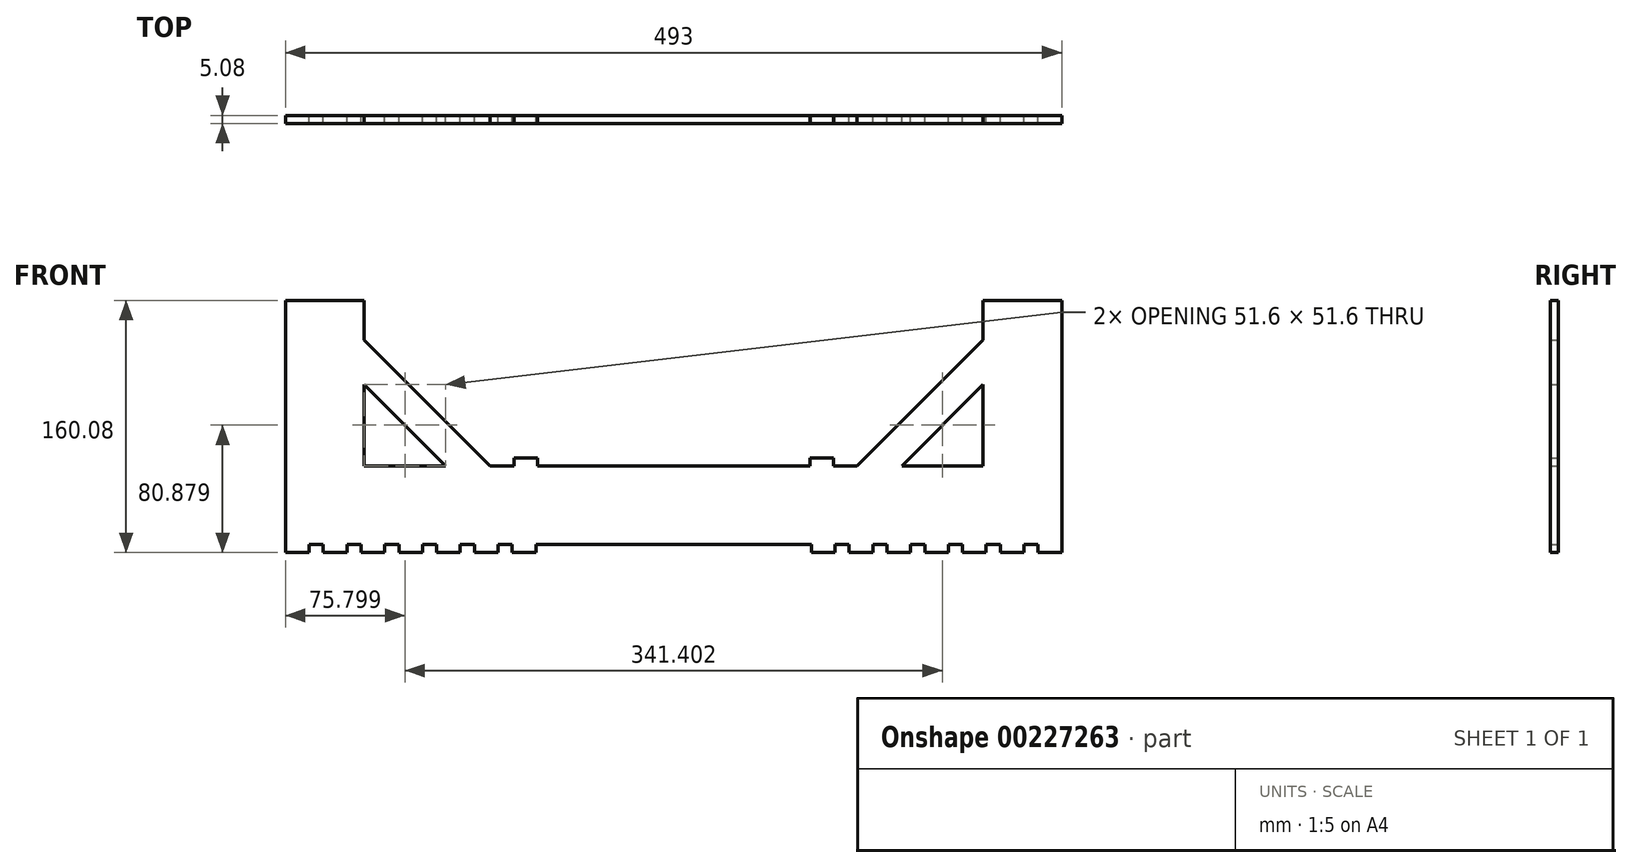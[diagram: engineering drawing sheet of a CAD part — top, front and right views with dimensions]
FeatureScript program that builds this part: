
annotation { "Feature Type Name" : "Feature", "Feature Type Description" : "" }
export const myFeature = defineFeature(function(context is Context, id is Id, definition is map)
    precondition{}
    {
        {
            var Q0;
            Q0=qCreatedBy(makeId("Front.planeOp"),FACE);
            var sketch = newSketch(context, id + "F0", { "sketchPlane" : qUnion([Q0])});
            skLineSegment(sketch, "E0", {"start": v(0, 0) * mm, "end": v(-246.5, 0) * mm});
            skLineSegment(sketch, "E1", {"start": v(-246.5, 0) * mm, "end": v(-246.5, 130) * mm});
            skLineSegment(sketch, "E2", {"start": v(-246.5, 130) * mm, "end": v(-196.5, 130) * mm});
            skLineSegment(sketch, "E3", {"start": v(-196.5, 130) * mm, "end": v(-196.5, 50) * mm});
            skLineSegment(sketch, "E4", {"start": v(-196.5, 50) * mm, "end": v(0, 50) * mm});
            skLineSegment(sketch, "E5", {"start": v(0, 50) * mm, "end": v(0, 0) * mm});
            skLineSegment(sketch, "E6", {"start": v(-196.5, 130) * mm, "end": v(-116.5, 50) * mm});
            skLineSegment(sketch, "E7", {"start": v(-196.5, 101.6) * mm, "end": v(-144.9, 50) * mm});
            skLineSegment(sketch, "E8", {"start": v(-246.5, 0) * mm, "end": v(-246.5, -5.08) * mm});
            skLineSegment(sketch, "E9", {"start": v(-246.5, -5.08) * mm, "end": v(-231.5, -5.08) * mm});
            skLineSegment(sketch, "E10", {"start": v(-231.5, -5.08) * mm, "end": v(-231.5, 0) * mm});
            skLineSegment(sketch, "E11.MirrorCS", {"start": v(196.5, 50) * mm, "end": v(0, 50) * mm});
            skLineSegment(sketch, "E12.MirrorCS", {"start": v(196.5, 130) * mm, "end": v(196.5, 50) * mm});
            skLineSegment(sketch, "E13.MirrorCS", {"start": v(196.5, 130) * mm, "end": v(116.5, 50) * mm});
            skLineSegment(sketch, "E14.MirrorCS", {"start": v(196.5, 101.6) * mm, "end": v(144.9, 50) * mm});
            skLineSegment(sketch, "E15.MirrorCS", {"start": v(246.5, 130) * mm, "end": v(196.5, 130) * mm});
            skLineSegment(sketch, "E16.MirrorCS", {"start": v(0, 0) * mm, "end": v(246.5, 0) * mm});
            skLineSegment(sketch, "E17.MirrorCS", {"start": v(246.5, 0) * mm, "end": v(246.5, 130) * mm});
            skLineSegment(sketch, "E18.1.0.0", {"start": v(-207.5, -5.08) * mm, "end": v(-207.5, 0) * mm});
            skLineSegment(sketch, "E18.1.0.1", {"start": v(-222.5, -5.08) * mm, "end": v(-207.5, -5.08) * mm});
            skLineSegment(sketch, "E18.1.0.2", {"start": v(-222.5, 0) * mm, "end": v(-222.5, -5.08) * mm});
            skLineSegment(sketch, "E18.2.0.0", {"start": v(-183.5, -5.08) * mm, "end": v(-183.5, 0) * mm});
            skLineSegment(sketch, "E18.2.0.1", {"start": v(-198.5, -5.08) * mm, "end": v(-183.5, -5.08) * mm});
            skLineSegment(sketch, "E18.2.0.2", {"start": v(-198.5, 0) * mm, "end": v(-198.5, -5.08) * mm});
            skLineSegment(sketch, "E18.3.0.0", {"start": v(-159.5, -5.08) * mm, "end": v(-159.5, 0) * mm});
            skLineSegment(sketch, "E18.3.0.1", {"start": v(-174.5, -5.08) * mm, "end": v(-159.5, -5.08) * mm});
            skLineSegment(sketch, "E18.3.0.2", {"start": v(-174.5, 0) * mm, "end": v(-174.5, -5.08) * mm});
            skLineSegment(sketch, "E18.4.0.0", {"start": v(-135.5, -5.08) * mm, "end": v(-135.5, 0) * mm});
            skLineSegment(sketch, "E18.4.0.1", {"start": v(-150.5, -5.08) * mm, "end": v(-135.5, -5.08) * mm});
            skLineSegment(sketch, "E18.4.0.2", {"start": v(-150.5, 0) * mm, "end": v(-150.5, -5.08) * mm});
            skLineSegment(sketch, "E18.5.0.0", {"start": v(-111.5, -5.08) * mm, "end": v(-111.5, 0) * mm});
            skLineSegment(sketch, "E18.5.0.1", {"start": v(-126.5, -5.08) * mm, "end": v(-111.5, -5.08) * mm});
            skLineSegment(sketch, "E18.5.0.2", {"start": v(-126.5, 0) * mm, "end": v(-126.5, -5.08) * mm});
            skLineSegment(sketch, "E18.6.0.0", {"start": v(-87.5, -5.08) * mm, "end": v(-87.5, 0) * mm});
            skLineSegment(sketch, "E18.6.0.1", {"start": v(-102.5, -5.08) * mm, "end": v(-87.5, -5.08) * mm});
            skLineSegment(sketch, "E18.6.0.2", {"start": v(-102.5, 0) * mm, "end": v(-102.5, -5.08) * mm});
            skLineSegment(sketch, "E18.direction1", {"start": v(-246.5, -5.08) * mm, "end": v(-222.5, -5.08) * mm, "construction": true});
            skLineSegment(sketch, "E19.MirrorCS", {"start": v(246.5, 0) * mm, "end": v(246.5, -5.08) * mm});
            skLineSegment(sketch, "E20.MirrorCS", {"start": v(231.5, -5.08) * mm, "end": v(231.5, 0) * mm});
            skLineSegment(sketch, "E21.MirrorCS", {"start": v(222.5, 0) * mm, "end": v(222.5, -5.08) * mm});
            skLineSegment(sketch, "E22.MirrorCS", {"start": v(222.5, -5.08) * mm, "end": v(207.5, -5.08) * mm});
            skLineSegment(sketch, "E23.MirrorCS", {"start": v(207.5, -5.08) * mm, "end": v(207.5, 0) * mm});
            skLineSegment(sketch, "E24.MirrorCS", {"start": v(198.5, 0) * mm, "end": v(198.5, -5.08) * mm});
            skLineSegment(sketch, "E25.MirrorCS", {"start": v(198.5, -5.08) * mm, "end": v(183.5, -5.08) * mm});
            skLineSegment(sketch, "E26.MirrorCS", {"start": v(183.5, -5.08) * mm, "end": v(183.5, 0) * mm});
            skLineSegment(sketch, "E27.MirrorCS", {"start": v(174.5, 0) * mm, "end": v(174.5, -5.08) * mm});
            skLineSegment(sketch, "E28.MirrorCS", {"start": v(174.5, -5.08) * mm, "end": v(159.5, -5.08) * mm});
            skLineSegment(sketch, "E29.MirrorCS", {"start": v(159.5, -5.08) * mm, "end": v(159.5, 0) * mm});
            skLineSegment(sketch, "E30.MirrorCS", {"start": v(150.5, 0) * mm, "end": v(150.5, -5.08) * mm});
            skLineSegment(sketch, "E31.MirrorCS", {"start": v(150.5, -5.08) * mm, "end": v(135.5, -5.08) * mm});
            skLineSegment(sketch, "E32.MirrorCS", {"start": v(135.5, -5.08) * mm, "end": v(135.5, 0) * mm});
            skLineSegment(sketch, "E33.MirrorCS", {"start": v(87.5, -5.08) * mm, "end": v(87.5, 0) * mm});
            skLineSegment(sketch, "E34.MirrorCS", {"start": v(102.5, -5.08) * mm, "end": v(87.5, -5.08) * mm});
            skLineSegment(sketch, "E35.MirrorCS", {"start": v(102.5, 0) * mm, "end": v(102.5, -5.08) * mm});
            skLineSegment(sketch, "E36.MirrorCS", {"start": v(111.5, -5.08) * mm, "end": v(111.5, 0) * mm});
            skLineSegment(sketch, "E37.MirrorCS", {"start": v(126.5, 0) * mm, "end": v(126.5, -5.08) * mm});
            skLineSegment(sketch, "E38.MirrorCS", {"start": v(126.5, -5.08) * mm, "end": v(111.5, -5.08) * mm});
            skLineSegment(sketch, "E39", {"start": v(231.5, -5.08) * mm, "end": v(246.5, -5.08) * mm});
            skSolve(sketch);
        }
        {
            var Q0;
            Q0 = qSketchRegion(id + "F0", true);
            extrude(context, id + "F1", {"entities" : qUnion([Q0]), "depth" : 5.08 * mm});
        }
        {
            var Q0;
            Q0=makeQuery(id+"F1.opExtrude","SWEPT_FACE",FACE,{"disambiguationData":[OSD([sQuery(id+"F0.wireOp",EDGE,"E2")])]});
            var Q1;
            Q1=makeQuery(id+"F1.opExtrude","SWEPT_FACE",FACE,{"disambiguationData":[OSD([sQuery(id+"F0.wireOp",EDGE,"E15.MirrorCS")])]});
            extrude(context, id + "F2", {"entities" : qUnion([Q0, Q1]), "operationType" : NewBodyOperationType.ADD, "depth" : 25 * mm});
        }
        {
            var Q0;
            Q0=makeQuery(id+"F1.opExtrude","SWEPT_FACE",FACE,{"disambiguationData":[OSD([sQuery(id+"F0.wireOp",EDGE,"E4"),sQuery(id+"F0.wireOp",EDGE,"E11.MirrorCS")])]});
            var sketch = newSketch(context, id + "F3", { "sketchPlane" : qUnion([Q0])});
            skLineSegment(sketch, "E40.bottom", {"start": v(101.5, -5.08) * mm, "end": v(86.5, -5.08) * mm});
            skLineSegment(sketch, "E40.top", {"start": v(101.5, 0) * mm, "end": v(86.5, 0) * mm});
            skLineSegment(sketch, "E40.right", {"start": v(86.5, -5.08) * mm, "end": v(86.5, 0) * mm});
            skLineSegment(sketch, "E41", {"start": v(101.5, -5.08) * mm, "end": v(101.5, 0) * mm});
            skPoint(sketch, "E40.left.start.orphan", {"position": v(116.5, -5.08) * mm});
            skPoint(sketch, "E42.orphan", {"position": v(116.5, 0) * mm});
            skSolve(sketch);
        }
        {
            var Q0;
            Q0 = qSketchRegion(id + "F3", true);
            extrude(context, id + "F4", {"entities" : qUnion([Q0]), "operationType" : NewBodyOperationType.ADD, "depth" : 5.08 * mm});
        }
        {
            var Q0;
            {var subQ1=sQuery(id+"F0.wireOp",EDGE,"E6");var subQ47=sQuery(id+"F0.wireOp",EDGE,"E11.MirrorCS");var subQ52=sQuery(id+"F0.wireOp",EDGE,"E4");Q0=makeQuery(id+"F4.boolean.opBoolean","SPLIT",FACE,{"disambiguationData":[TD([makeQuery(id+"F1.opExtrude","SWEPT_FACE",FACE,{"disambiguationData":[OSD([subQ1])]})])],"derivedFrom":makeQuery(id+"F1.opExtrude","SWEPT_FACE",FACE,{"disambiguationData":[OSD([subQ52,subQ47])]})});}
            var sketch = newSketch(context, id + "F5", { "sketchPlane" : qUnion([Q0])});
            skLineSegment(sketch, "E43.bottom", {"start": v(-101.5, -5.08) * mm, "end": v(-86.5, -5.08) * mm});
            skLineSegment(sketch, "E43.top", {"start": v(-101.5, 0) * mm, "end": v(-86.5, 0) * mm});
            skLineSegment(sketch, "E43.right", {"start": v(-86.5, -5.08) * mm, "end": v(-86.5, 0) * mm});
            skLineSegment(sketch, "E44", {"start": v(-101.5, -5.08) * mm, "end": v(-101.5, 0) * mm});
            skPoint(sketch, "E43.left.start.orphan", {"position": v(-116.5, -5.08) * mm});
            skPoint(sketch, "E45.orphan", {"position": v(-116.5, 0) * mm});
            skSolve(sketch);
        }
        {
            var Q0;
            Q0 = qSketchRegion(id + "F5", true);
            extrude(context, id + "F6", {"entities" : qUnion([Q0]), "operationType" : NewBodyOperationType.ADD, "depth" : 5.08 * mm});
        }
    });
